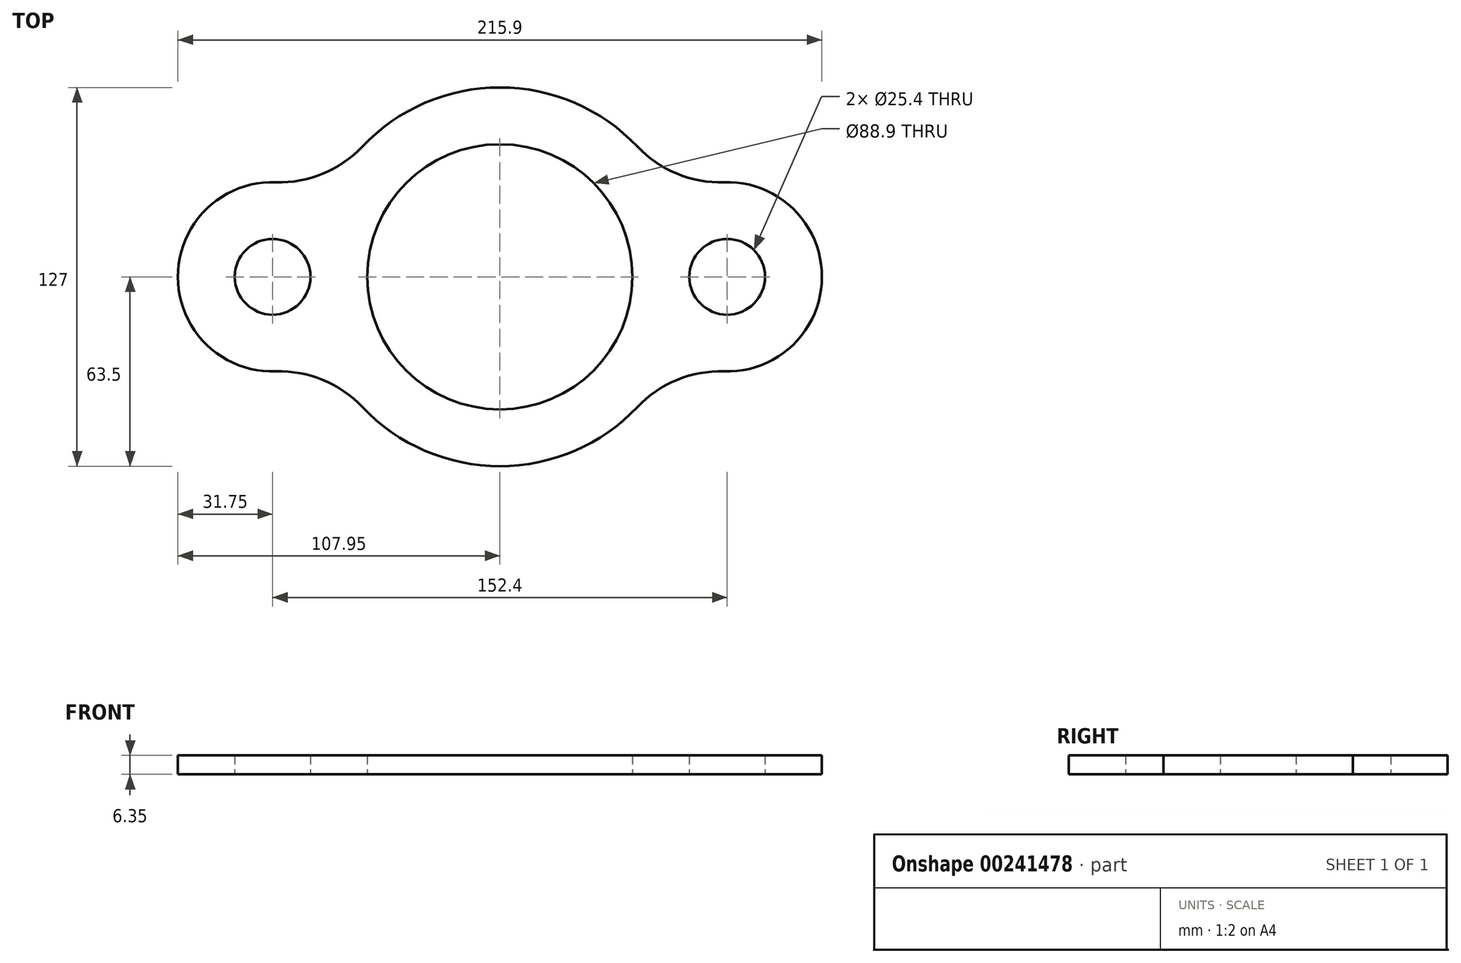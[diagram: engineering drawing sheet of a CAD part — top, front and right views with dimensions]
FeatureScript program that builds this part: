
annotation { "Feature Type Name" : "Feature", "Feature Type Description" : "" }
export const myFeature = defineFeature(function(context is Context, id is Id, definition is map)
    precondition{}
    {
        {
            var Q0;
            Q0=qCreatedBy(makeId("Top.planeOp"),FACE);
            var sketch = newSketch(context, id + "F0", { "sketchPlane" : qUnion([Q0])});
            skCircle(sketch, "E0", {"center": v(0, 0) * mm, "radius": 44.45 * mm});
            skArc(sketch, "E1", {"start": v(-46.14, -43.63) * mm, "mid": v(0, -63.5) * mm, "end": v(46.14, -43.63) * mm});
            skCircle(sketch, "E2", {"center": v(76.2, 0) * mm, "radius": 12.7 * mm});
            skArc(sketch, "E3", {"start": v(75.12, -31.73) * mm, "mid": v(107.95, 0) * mm, "end": v(75.12, 31.73) * mm});
            skCircle(sketch, "E4", {"center": v(-76.2, 0) * mm, "radius": 12.7 * mm});
            skArc(sketch, "E5", {"start": v(-75.12, 31.73) * mm, "mid": v(-107.95, 0) * mm, "end": v(-75.12, -31.73) * mm});
            skArc(sketch, "E6.trimOffspring", {"start": v(46.14, 43.63) * mm, "mid": v(0, 63.5) * mm, "end": v(-46.14, 43.63) * mm});
            skPoint(sketch, "E7.visualSharp", {"position": v(-57.94, 25.98) * mm});
            skArc(sketch, "E7.filletArc", {"start": v(-75.12, 31.73) * mm, "mid": v(-59.35, 34.56) * mm, "end": v(-46.14, 43.63) * mm});
            skPoint(sketch, "E8.visualSharp", {"position": v(57.94, 25.98) * mm});
            skArc(sketch, "E8.filletArc", {"start": v(46.14, 43.63) * mm, "mid": v(59.35, 34.56) * mm, "end": v(75.12, 31.73) * mm});
            skPoint(sketch, "E9.visualSharp", {"position": v(57.94, -25.98) * mm});
            skArc(sketch, "E9.filletArc", {"start": v(75.12, -31.73) * mm, "mid": v(59.35, -34.56) * mm, "end": v(46.14, -43.63) * mm});
            skPoint(sketch, "E10.visualSharp", {"position": v(-57.94, -25.98) * mm});
            skArc(sketch, "E10.filletArc", {"start": v(-46.14, -43.63) * mm, "mid": v(-59.35, -34.56) * mm, "end": v(-75.12, -31.73) * mm});
            skSolve(sketch);
        }
        {
            var Q0;
            Q0 = qSketchRegion(id + "F0", true);
            extrude(context, id + "F1", {"entities" : qUnion([Q0]), "depth" : 6.35 * mm});
        }
    });
